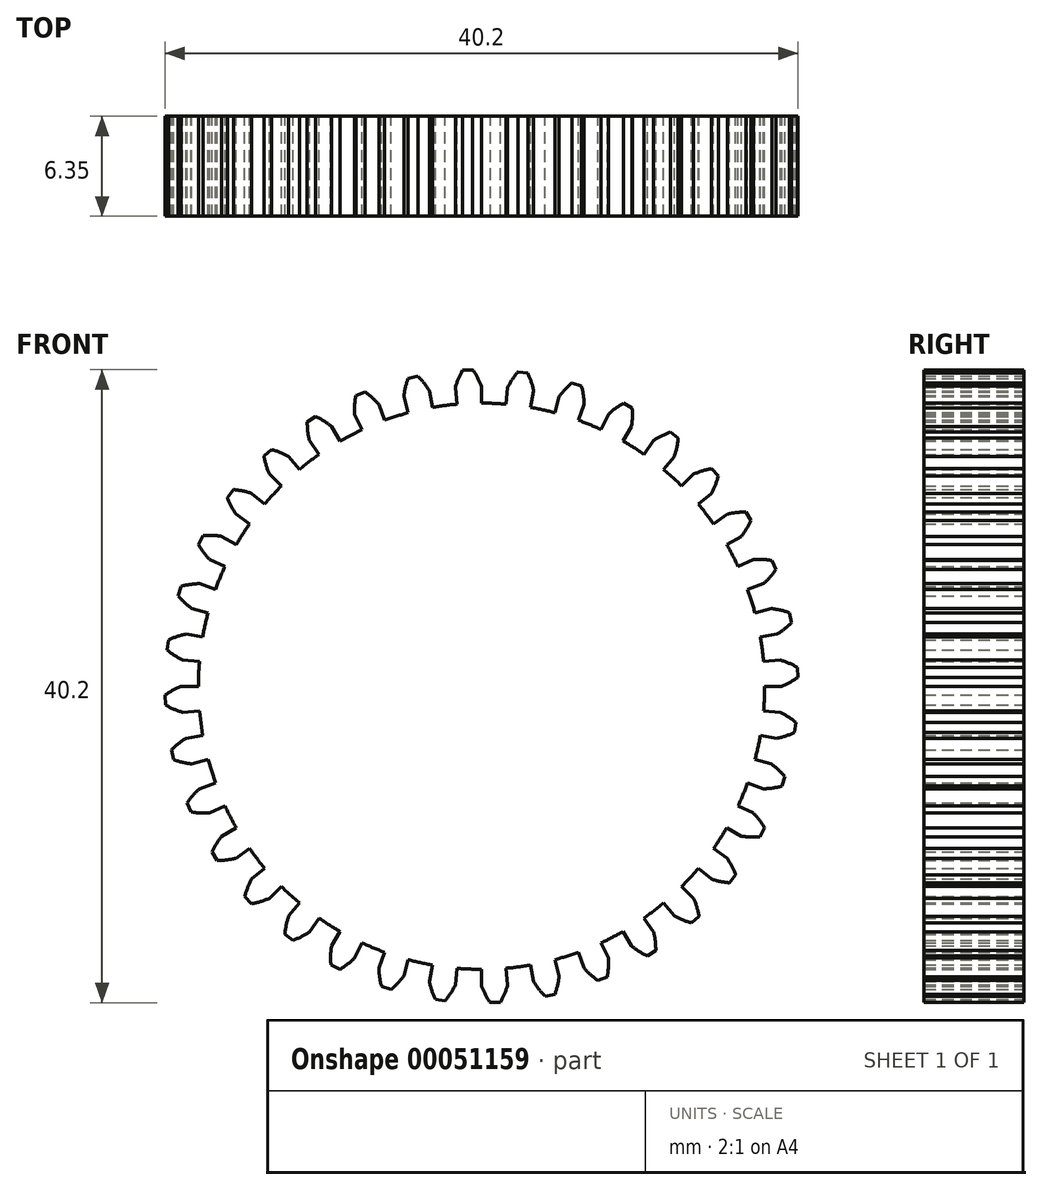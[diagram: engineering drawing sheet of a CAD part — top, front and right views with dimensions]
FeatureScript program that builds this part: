
annotation { "Feature Type Name" : "Feature", "Feature Type Description" : "" }
export const myFeature = defineFeature(function(context is Context, id is Id, definition is map)
    precondition{}
    {
        {
            var Q0;
            Q0=qCreatedBy(makeId("Front.planeOp"),FACE);
            var sketch = newSketch(context, id + "F0", { "sketchPlane" : qUnion([Q0])});
            skArc(sketch, "E0", {"start": v(1.57, 17.91) * mm, "mid": v(0.78, 17.97) * mm, "end": v(0, 17.98) * mm});
            skLineSegment(sketch, "E1", {"start": v(0, 19.05) * mm, "end": v(0, 17.98) * mm, "construction": true});
            skArc(sketch, "E2", {"start": v(-4.48, 17.42) * mm, "mid": v(-4.46, 17.38) * mm, "end": v(-4.45, 17.34) * mm});
            skArc(sketch, "E3.trimOffspring", {"start": v(0, 19.05) * mm, "mid": v(-0.25, 19.6) * mm, "end": v(-0.56, 20.1) * mm});
            skLineSegment(sketch, "E4", {"start": v(-0.56, 20.1) * mm, "end": v(-0.88, 20.08) * mm});
            skLineSegment(sketch, "E5", {"start": v(0, 19.05) * mm, "end": v(0, 17.98) * mm});
            skLineSegment(sketch, "E6.MirrorCS", {"start": v(-1.2, 20.07) * mm, "end": v(-0.88, 20.08) * mm});
            skArc(sketch, "E7.MirrorCS", {"start": v(-1.66, 18.98) * mm, "mid": v(-1.46, 19.54) * mm, "end": v(-1.2, 20.07) * mm});
            skLineSegment(sketch, "E8.MirrorCS", {"start": v(-1.66, 18.98) * mm, "end": v(-1.57, 17.91) * mm});
            skArc(sketch, "E9.1.0", {"start": v(-3.3, 18.76) * mm, "mid": v(-3.65, 19.25) * mm, "end": v(-4.04, 19.7) * mm});
            skLineSegment(sketch, "E9.1.1", {"start": v(-4.04, 19.7) * mm, "end": v(-4.35, 19.63) * mm});
            skLineSegment(sketch, "E9.1.2", {"start": v(-4.66, 19.56) * mm, "end": v(-4.35, 19.63) * mm});
            skArc(sketch, "E9.1.3", {"start": v(-4.93, 18.4) * mm, "mid": v(-4.83, 18.99) * mm, "end": v(-4.66, 19.56) * mm});
            skLineSegment(sketch, "E9.1.4", {"start": v(-4.93, 18.4) * mm, "end": v(-4.65, 17.37) * mm});
            skLineSegment(sketch, "E9.1.5", {"start": v(-3.3, 18.76) * mm, "end": v(-3.12, 17.7) * mm});
            skArc(sketch, "E9.2.0", {"start": v(-6.52, 17.9) * mm, "mid": v(-6.93, 18.32) * mm, "end": v(-7.4, 18.7) * mm});
            skLineSegment(sketch, "E9.2.1", {"start": v(-7.4, 18.7) * mm, "end": v(-7.7, 18.57) * mm});
            skLineSegment(sketch, "E9.2.2", {"start": v(-7.98, 18.45) * mm, "end": v(-7.7, 18.57) * mm});
            skArc(sketch, "E9.2.3", {"start": v(-8.05, 17.27) * mm, "mid": v(-8.05, 17.86) * mm, "end": v(-7.98, 18.45) * mm});
            skLineSegment(sketch, "E9.2.4", {"start": v(-8.05, 17.27) * mm, "end": v(-7.6, 16.3) * mm});
            skLineSegment(sketch, "E9.2.5", {"start": v(-6.52, 17.9) * mm, "end": v(-6.15, 16.9) * mm});
            skArc(sketch, "E9.3.0", {"start": v(-9.52, 16.5) * mm, "mid": v(-10, 16.84) * mm, "end": v(-10.53, 17.12) * mm});
            skLineSegment(sketch, "E9.3.1", {"start": v(-10.53, 17.12) * mm, "end": v(-10.8, 16.95) * mm});
            skLineSegment(sketch, "E9.3.2", {"start": v(-11.07, 16.78) * mm, "end": v(-10.8, 16.95) * mm});
            skArc(sketch, "E9.3.3", {"start": v(-10.93, 15.6) * mm, "mid": v(-11.03, 16.19) * mm, "end": v(-11.07, 16.78) * mm});
            skLineSegment(sketch, "E9.3.4", {"start": v(-10.93, 15.6) * mm, "end": v(-10.31, 14.73) * mm});
            skLineSegment(sketch, "E9.3.5", {"start": v(-9.52, 16.5) * mm, "end": v(-9, 15.57) * mm});
            skArc(sketch, "E9.4.0", {"start": v(-12.25, 14.6) * mm, "mid": v(-12.78, 14.85) * mm, "end": v(-13.35, 15.03) * mm});
            skLineSegment(sketch, "E9.4.1", {"start": v(-13.35, 15.03) * mm, "end": v(-13.58, 14.82) * mm});
            skLineSegment(sketch, "E9.4.2", {"start": v(-13.81, 14.6) * mm, "end": v(-13.58, 14.82) * mm});
            skArc(sketch, "E9.4.3", {"start": v(-13.47, 13.47) * mm, "mid": v(-13.68, 14.03) * mm, "end": v(-13.81, 14.6) * mm});
            skLineSegment(sketch, "E9.4.4", {"start": v(-13.47, 13.47) * mm, "end": v(-12.72, 12.72) * mm});
            skLineSegment(sketch, "E9.4.5", {"start": v(-12.25, 14.6) * mm, "end": v(-11.56, 13.78) * mm});
            skArc(sketch, "E9.5.0", {"start": v(-14.6, 12.25) * mm, "mid": v(-15.17, 12.4) * mm, "end": v(-15.76, 12.49) * mm});
            skLineSegment(sketch, "E9.5.1", {"start": v(-15.76, 12.49) * mm, "end": v(-15.95, 12.24) * mm});
            skLineSegment(sketch, "E9.5.2", {"start": v(-16.14, 11.99) * mm, "end": v(-15.95, 12.24) * mm});
            skArc(sketch, "E9.5.3", {"start": v(-15.6, 10.93) * mm, "mid": v(-15.9, 11.44) * mm, "end": v(-16.14, 11.99) * mm});
            skLineSegment(sketch, "E9.5.4", {"start": v(-15.6, 10.93) * mm, "end": v(-14.73, 10.31) * mm});
            skLineSegment(sketch, "E9.5.5", {"start": v(-14.6, 12.25) * mm, "end": v(-13.78, 11.56) * mm});
            skArc(sketch, "E9.6.0", {"start": v(-16.5, 9.53) * mm, "mid": v(-17.09, 9.58) * mm, "end": v(-17.68, 9.56) * mm});
            skLineSegment(sketch, "E9.6.1", {"start": v(-17.68, 9.56) * mm, "end": v(-17.83, 9.28) * mm});
            skLineSegment(sketch, "E9.6.2", {"start": v(-17.98, 9) * mm, "end": v(-17.83, 9.28) * mm});
            skArc(sketch, "E9.6.3", {"start": v(-17.27, 8.05) * mm, "mid": v(-17.65, 8.5) * mm, "end": v(-17.98, 9) * mm});
            skLineSegment(sketch, "E9.6.4", {"start": v(-17.27, 8.05) * mm, "end": v(-16.3, 7.6) * mm});
            skLineSegment(sketch, "E9.6.5", {"start": v(-16.5, 9.53) * mm, "end": v(-15.57, 9) * mm});
            skArc(sketch, "E9.7.0", {"start": v(-17.9, 6.52) * mm, "mid": v(-18.5, 6.47) * mm, "end": v(-19.08, 6.35) * mm});
            skLineSegment(sketch, "E9.7.1", {"start": v(-19.08, 6.35) * mm, "end": v(-19.17, 6.04) * mm});
            skLineSegment(sketch, "E9.7.2", {"start": v(-19.27, 5.74) * mm, "end": v(-19.17, 6.04) * mm});
            skArc(sketch, "E9.7.3", {"start": v(-18.4, 4.93) * mm, "mid": v(-18.86, 5.3) * mm, "end": v(-19.27, 5.74) * mm});
            skLineSegment(sketch, "E9.7.4", {"start": v(-18.4, 4.93) * mm, "end": v(-17.37, 4.65) * mm});
            skLineSegment(sketch, "E9.7.5", {"start": v(-17.9, 6.52) * mm, "end": v(-16.9, 6.15) * mm});
            skArc(sketch, "E9.8.0", {"start": v(-18.76, 3.3) * mm, "mid": v(-19.34, 3.16) * mm, "end": v(-19.89, 2.94) * mm});
            skLineSegment(sketch, "E9.8.1", {"start": v(-19.89, 2.94) * mm, "end": v(-19.93, 2.62) * mm});
            skLineSegment(sketch, "E9.8.2", {"start": v(-19.97, 2.31) * mm, "end": v(-19.93, 2.62) * mm});
            skArc(sketch, "E9.8.3", {"start": v(-18.98, 1.66) * mm, "mid": v(-19.5, 1.95) * mm, "end": v(-19.97, 2.31) * mm});
            skLineSegment(sketch, "E9.8.4", {"start": v(-18.98, 1.66) * mm, "end": v(-17.91, 1.57) * mm});
            skLineSegment(sketch, "E9.8.5", {"start": v(-18.76, 3.3) * mm, "end": v(-17.7, 3.12) * mm});
            skArc(sketch, "E9.9.0", {"start": v(-19.05, 0) * mm, "mid": v(-19.6, -0.25) * mm, "end": v(-20.1, -0.56) * mm});
            skLineSegment(sketch, "E9.9.1", {"start": v(-20.1, -0.56) * mm, "end": v(-20.08, -0.88) * mm});
            skLineSegment(sketch, "E9.9.2", {"start": v(-20.07, -1.2) * mm, "end": v(-20.08, -0.88) * mm});
            skArc(sketch, "E9.9.3", {"start": v(-18.98, -1.66) * mm, "mid": v(-19.54, -1.46) * mm, "end": v(-20.07, -1.2) * mm});
            skLineSegment(sketch, "E9.9.4", {"start": v(-18.98, -1.66) * mm, "end": v(-17.91, -1.57) * mm});
            skLineSegment(sketch, "E9.9.5", {"start": v(-19.05, 0) * mm, "end": v(-17.98, 0) * mm});
            skArc(sketch, "E9.10.0", {"start": v(-18.76, -3.3) * mm, "mid": v(-19.25, -3.65) * mm, "end": v(-19.7, -4.04) * mm});
            skLineSegment(sketch, "E9.10.1", {"start": v(-19.7, -4.04) * mm, "end": v(-19.63, -4.35) * mm});
            skLineSegment(sketch, "E9.10.2", {"start": v(-19.56, -4.66) * mm, "end": v(-19.63, -4.35) * mm});
            skArc(sketch, "E9.10.3", {"start": v(-18.4, -4.93) * mm, "mid": v(-18.99, -4.83) * mm, "end": v(-19.56, -4.66) * mm});
            skLineSegment(sketch, "E9.10.4", {"start": v(-18.4, -4.93) * mm, "end": v(-17.37, -4.65) * mm});
            skLineSegment(sketch, "E9.10.5", {"start": v(-18.76, -3.3) * mm, "end": v(-17.7, -3.12) * mm});
            skArc(sketch, "E9.11.0", {"start": v(-17.9, -6.52) * mm, "mid": v(-18.32, -6.93) * mm, "end": v(-18.7, -7.4) * mm});
            skLineSegment(sketch, "E9.11.1", {"start": v(-18.7, -7.4) * mm, "end": v(-18.57, -7.7) * mm});
            skLineSegment(sketch, "E9.11.2", {"start": v(-18.45, -7.98) * mm, "end": v(-18.57, -7.7) * mm});
            skArc(sketch, "E9.11.3", {"start": v(-17.27, -8.05) * mm, "mid": v(-17.86, -8.05) * mm, "end": v(-18.45, -7.98) * mm});
            skLineSegment(sketch, "E9.11.4", {"start": v(-17.27, -8.05) * mm, "end": v(-16.3, -7.6) * mm});
            skLineSegment(sketch, "E9.11.5", {"start": v(-17.9, -6.52) * mm, "end": v(-16.9, -6.15) * mm});
            skArc(sketch, "E9.12.0", {"start": v(-16.5, -9.52) * mm, "mid": v(-16.84, -10) * mm, "end": v(-17.12, -10.53) * mm});
            skLineSegment(sketch, "E9.12.1", {"start": v(-17.12, -10.53) * mm, "end": v(-16.95, -10.8) * mm});
            skLineSegment(sketch, "E9.12.2", {"start": v(-16.78, -11.07) * mm, "end": v(-16.95, -10.8) * mm});
            skArc(sketch, "E9.12.3", {"start": v(-15.6, -10.93) * mm, "mid": v(-16.19, -11.03) * mm, "end": v(-16.78, -11.07) * mm});
            skLineSegment(sketch, "E9.12.4", {"start": v(-15.6, -10.93) * mm, "end": v(-14.73, -10.31) * mm});
            skLineSegment(sketch, "E9.12.5", {"start": v(-16.5, -9.52) * mm, "end": v(-15.57, -9) * mm});
            skArc(sketch, "E9.13.0", {"start": v(-14.6, -12.25) * mm, "mid": v(-14.85, -12.78) * mm, "end": v(-15.03, -13.35) * mm});
            skLineSegment(sketch, "E9.13.1", {"start": v(-15.03, -13.35) * mm, "end": v(-14.82, -13.58) * mm});
            skLineSegment(sketch, "E9.13.2", {"start": v(-14.6, -13.81) * mm, "end": v(-14.82, -13.58) * mm});
            skArc(sketch, "E9.13.3", {"start": v(-13.47, -13.47) * mm, "mid": v(-14.03, -13.68) * mm, "end": v(-14.6, -13.81) * mm});
            skLineSegment(sketch, "E9.13.4", {"start": v(-13.47, -13.47) * mm, "end": v(-12.72, -12.72) * mm});
            skLineSegment(sketch, "E9.13.5", {"start": v(-14.6, -12.25) * mm, "end": v(-13.78, -11.56) * mm});
            skArc(sketch, "E9.14.0", {"start": v(-12.25, -14.6) * mm, "mid": v(-12.4, -15.17) * mm, "end": v(-12.49, -15.76) * mm});
            skLineSegment(sketch, "E9.14.1", {"start": v(-12.49, -15.76) * mm, "end": v(-12.24, -15.95) * mm});
            skLineSegment(sketch, "E9.14.2", {"start": v(-11.99, -16.14) * mm, "end": v(-12.24, -15.95) * mm});
            skArc(sketch, "E9.14.3", {"start": v(-10.93, -15.6) * mm, "mid": v(-11.44, -15.9) * mm, "end": v(-11.99, -16.14) * mm});
            skLineSegment(sketch, "E9.14.4", {"start": v(-10.93, -15.6) * mm, "end": v(-10.31, -14.73) * mm});
            skLineSegment(sketch, "E9.14.5", {"start": v(-12.25, -14.6) * mm, "end": v(-11.56, -13.78) * mm});
            skArc(sketch, "E9.15.0", {"start": v(-9.53, -16.5) * mm, "mid": v(-9.58, -17.09) * mm, "end": v(-9.56, -17.68) * mm});
            skLineSegment(sketch, "E9.15.1", {"start": v(-9.56, -17.68) * mm, "end": v(-9.28, -17.83) * mm});
            skLineSegment(sketch, "E9.15.2", {"start": v(-9, -17.98) * mm, "end": v(-9.28, -17.83) * mm});
            skArc(sketch, "E9.15.3", {"start": v(-8.05, -17.27) * mm, "mid": v(-8.5, -17.65) * mm, "end": v(-9, -17.98) * mm});
            skLineSegment(sketch, "E9.15.4", {"start": v(-8.05, -17.27) * mm, "end": v(-7.6, -16.3) * mm});
            skLineSegment(sketch, "E9.15.5", {"start": v(-9.53, -16.5) * mm, "end": v(-9, -15.57) * mm});
            skArc(sketch, "E9.16.0", {"start": v(-6.52, -17.9) * mm, "mid": v(-6.47, -18.5) * mm, "end": v(-6.35, -19.08) * mm});
            skLineSegment(sketch, "E9.16.1", {"start": v(-6.35, -19.08) * mm, "end": v(-6.04, -19.17) * mm});
            skLineSegment(sketch, "E9.16.2", {"start": v(-5.74, -19.27) * mm, "end": v(-6.04, -19.17) * mm});
            skArc(sketch, "E9.16.3", {"start": v(-4.93, -18.4) * mm, "mid": v(-5.3, -18.86) * mm, "end": v(-5.74, -19.27) * mm});
            skLineSegment(sketch, "E9.16.4", {"start": v(-4.93, -18.4) * mm, "end": v(-4.65, -17.37) * mm});
            skLineSegment(sketch, "E9.16.5", {"start": v(-6.52, -17.9) * mm, "end": v(-6.15, -16.9) * mm});
            skArc(sketch, "E9.17.0", {"start": v(-3.3, -18.76) * mm, "mid": v(-3.16, -19.34) * mm, "end": v(-2.94, -19.89) * mm});
            skLineSegment(sketch, "E9.17.1", {"start": v(-2.94, -19.89) * mm, "end": v(-2.62, -19.93) * mm});
            skLineSegment(sketch, "E9.17.2", {"start": v(-2.31, -19.97) * mm, "end": v(-2.62, -19.93) * mm});
            skArc(sketch, "E9.17.3", {"start": v(-1.66, -18.98) * mm, "mid": v(-1.95, -19.5) * mm, "end": v(-2.31, -19.97) * mm});
            skLineSegment(sketch, "E9.17.4", {"start": v(-1.66, -18.98) * mm, "end": v(-1.57, -17.91) * mm});
            skLineSegment(sketch, "E9.17.5", {"start": v(-3.3, -18.76) * mm, "end": v(-3.12, -17.7) * mm});
            skArc(sketch, "E9.18.0", {"start": v(0, -19.05) * mm, "mid": v(0.25, -19.6) * mm, "end": v(0.56, -20.1) * mm});
            skLineSegment(sketch, "E9.18.1", {"start": v(0.56, -20.1) * mm, "end": v(0.88, -20.08) * mm});
            skLineSegment(sketch, "E9.18.2", {"start": v(1.2, -20.07) * mm, "end": v(0.88, -20.08) * mm});
            skArc(sketch, "E9.18.3", {"start": v(1.66, -18.98) * mm, "mid": v(1.46, -19.54) * mm, "end": v(1.2, -20.07) * mm});
            skLineSegment(sketch, "E9.18.4", {"start": v(1.66, -18.98) * mm, "end": v(1.57, -17.91) * mm});
            skLineSegment(sketch, "E9.18.5", {"start": v(0, -19.05) * mm, "end": v(0, -17.98) * mm});
            skArc(sketch, "E9.19.0", {"start": v(3.3, -18.76) * mm, "mid": v(3.65, -19.25) * mm, "end": v(4.04, -19.7) * mm});
            skLineSegment(sketch, "E9.19.1", {"start": v(4.04, -19.7) * mm, "end": v(4.35, -19.63) * mm});
            skLineSegment(sketch, "E9.19.2", {"start": v(4.66, -19.56) * mm, "end": v(4.35, -19.63) * mm});
            skArc(sketch, "E9.19.3", {"start": v(4.93, -18.4) * mm, "mid": v(4.83, -18.99) * mm, "end": v(4.66, -19.56) * mm});
            skLineSegment(sketch, "E9.19.4", {"start": v(4.93, -18.4) * mm, "end": v(4.65, -17.37) * mm});
            skLineSegment(sketch, "E9.19.5", {"start": v(3.3, -18.76) * mm, "end": v(3.12, -17.7) * mm});
            skArc(sketch, "E9.20.0", {"start": v(6.52, -17.9) * mm, "mid": v(6.93, -18.32) * mm, "end": v(7.4, -18.7) * mm});
            skLineSegment(sketch, "E9.20.1", {"start": v(7.4, -18.7) * mm, "end": v(7.7, -18.57) * mm});
            skLineSegment(sketch, "E9.20.2", {"start": v(7.98, -18.45) * mm, "end": v(7.7, -18.57) * mm});
            skArc(sketch, "E9.20.3", {"start": v(8.05, -17.27) * mm, "mid": v(8.05, -17.86) * mm, "end": v(7.98, -18.45) * mm});
            skLineSegment(sketch, "E9.20.4", {"start": v(8.05, -17.27) * mm, "end": v(7.6, -16.3) * mm});
            skLineSegment(sketch, "E9.20.5", {"start": v(6.52, -17.9) * mm, "end": v(6.15, -16.9) * mm});
            skArc(sketch, "E9.21.0", {"start": v(9.53, -16.5) * mm, "mid": v(10, -16.84) * mm, "end": v(10.53, -17.12) * mm});
            skLineSegment(sketch, "E9.21.1", {"start": v(10.53, -17.12) * mm, "end": v(10.8, -16.95) * mm});
            skLineSegment(sketch, "E9.21.2", {"start": v(11.07, -16.78) * mm, "end": v(10.8, -16.95) * mm});
            skArc(sketch, "E9.21.3", {"start": v(10.93, -15.6) * mm, "mid": v(11.03, -16.19) * mm, "end": v(11.07, -16.78) * mm});
            skLineSegment(sketch, "E9.21.4", {"start": v(10.93, -15.6) * mm, "end": v(10.31, -14.73) * mm});
            skLineSegment(sketch, "E9.21.5", {"start": v(9.53, -16.5) * mm, "end": v(9, -15.57) * mm});
            skArc(sketch, "E9.22.0", {"start": v(12.25, -14.6) * mm, "mid": v(12.78, -14.85) * mm, "end": v(13.35, -15.03) * mm});
            skLineSegment(sketch, "E9.22.1", {"start": v(13.35, -15.03) * mm, "end": v(13.58, -14.82) * mm});
            skLineSegment(sketch, "E9.22.2", {"start": v(13.81, -14.6) * mm, "end": v(13.58, -14.82) * mm});
            skArc(sketch, "E9.22.3", {"start": v(13.47, -13.47) * mm, "mid": v(13.68, -14.03) * mm, "end": v(13.81, -14.6) * mm});
            skLineSegment(sketch, "E9.22.4", {"start": v(13.47, -13.47) * mm, "end": v(12.72, -12.72) * mm});
            skLineSegment(sketch, "E9.22.5", {"start": v(12.25, -14.6) * mm, "end": v(11.56, -13.78) * mm});
            skArc(sketch, "E9.23.0", {"start": v(14.6, -12.25) * mm, "mid": v(15.17, -12.4) * mm, "end": v(15.76, -12.49) * mm});
            skLineSegment(sketch, "E9.23.1", {"start": v(15.76, -12.49) * mm, "end": v(15.95, -12.24) * mm});
            skLineSegment(sketch, "E9.23.2", {"start": v(16.14, -11.99) * mm, "end": v(15.95, -12.24) * mm});
            skArc(sketch, "E9.23.3", {"start": v(15.6, -10.93) * mm, "mid": v(15.9, -11.44) * mm, "end": v(16.14, -11.99) * mm});
            skLineSegment(sketch, "E9.23.4", {"start": v(15.6, -10.93) * mm, "end": v(14.73, -10.31) * mm});
            skLineSegment(sketch, "E9.23.5", {"start": v(14.6, -12.25) * mm, "end": v(13.78, -11.56) * mm});
            skArc(sketch, "E9.24.0", {"start": v(16.5, -9.53) * mm, "mid": v(17.09, -9.58) * mm, "end": v(17.68, -9.56) * mm});
            skLineSegment(sketch, "E9.24.1", {"start": v(17.68, -9.56) * mm, "end": v(17.83, -9.28) * mm});
            skLineSegment(sketch, "E9.24.2", {"start": v(17.98, -9) * mm, "end": v(17.83, -9.28) * mm});
            skArc(sketch, "E9.24.3", {"start": v(17.27, -8.05) * mm, "mid": v(17.65, -8.5) * mm, "end": v(17.98, -9) * mm});
            skLineSegment(sketch, "E9.24.4", {"start": v(17.27, -8.05) * mm, "end": v(16.3, -7.6) * mm});
            skLineSegment(sketch, "E9.24.5", {"start": v(16.5, -9.53) * mm, "end": v(15.57, -9) * mm});
            skArc(sketch, "E9.25.0", {"start": v(17.9, -6.52) * mm, "mid": v(18.5, -6.47) * mm, "end": v(19.08, -6.35) * mm});
            skLineSegment(sketch, "E9.25.1", {"start": v(19.08, -6.35) * mm, "end": v(19.17, -6.04) * mm});
            skLineSegment(sketch, "E9.25.2", {"start": v(19.27, -5.74) * mm, "end": v(19.17, -6.04) * mm});
            skArc(sketch, "E9.25.3", {"start": v(18.4, -4.93) * mm, "mid": v(18.86, -5.3) * mm, "end": v(19.27, -5.74) * mm});
            skLineSegment(sketch, "E9.25.4", {"start": v(18.4, -4.93) * mm, "end": v(17.37, -4.65) * mm});
            skLineSegment(sketch, "E9.25.5", {"start": v(17.9, -6.52) * mm, "end": v(16.9, -6.15) * mm});
            skArc(sketch, "E9.26.0", {"start": v(18.76, -3.3) * mm, "mid": v(19.34, -3.16) * mm, "end": v(19.89, -2.94) * mm});
            skLineSegment(sketch, "E9.26.1", {"start": v(19.89, -2.94) * mm, "end": v(19.93, -2.62) * mm});
            skLineSegment(sketch, "E9.26.2", {"start": v(19.97, -2.31) * mm, "end": v(19.93, -2.62) * mm});
            skArc(sketch, "E9.26.3", {"start": v(18.98, -1.66) * mm, "mid": v(19.5, -1.95) * mm, "end": v(19.97, -2.31) * mm});
            skLineSegment(sketch, "E9.26.4", {"start": v(18.98, -1.66) * mm, "end": v(17.91, -1.57) * mm});
            skLineSegment(sketch, "E9.26.5", {"start": v(18.76, -3.3) * mm, "end": v(17.7, -3.12) * mm});
            skArc(sketch, "E9.27.0", {"start": v(19.05, 0) * mm, "mid": v(19.6, 0.25) * mm, "end": v(20.1, 0.56) * mm});
            skLineSegment(sketch, "E9.27.1", {"start": v(20.1, 0.56) * mm, "end": v(20.08, 0.88) * mm});
            skLineSegment(sketch, "E9.27.2", {"start": v(20.07, 1.2) * mm, "end": v(20.08, 0.88) * mm});
            skArc(sketch, "E9.27.3", {"start": v(18.98, 1.66) * mm, "mid": v(19.54, 1.46) * mm, "end": v(20.07, 1.2) * mm});
            skLineSegment(sketch, "E9.27.4", {"start": v(18.98, 1.66) * mm, "end": v(17.91, 1.57) * mm});
            skLineSegment(sketch, "E9.27.5", {"start": v(19.05, 0) * mm, "end": v(17.98, 0) * mm});
            skArc(sketch, "E9.28.0", {"start": v(18.76, 3.3) * mm, "mid": v(19.25, 3.65) * mm, "end": v(19.7, 4.04) * mm});
            skLineSegment(sketch, "E9.28.1", {"start": v(19.7, 4.04) * mm, "end": v(19.63, 4.35) * mm});
            skLineSegment(sketch, "E9.28.2", {"start": v(19.56, 4.66) * mm, "end": v(19.63, 4.35) * mm});
            skArc(sketch, "E9.28.3", {"start": v(18.4, 4.93) * mm, "mid": v(18.99, 4.83) * mm, "end": v(19.56, 4.66) * mm});
            skLineSegment(sketch, "E9.28.4", {"start": v(18.4, 4.93) * mm, "end": v(17.37, 4.65) * mm});
            skLineSegment(sketch, "E9.28.5", {"start": v(18.76, 3.3) * mm, "end": v(17.7, 3.12) * mm});
            skArc(sketch, "E9.29.0", {"start": v(17.9, 6.52) * mm, "mid": v(18.32, 6.93) * mm, "end": v(18.7, 7.4) * mm});
            skLineSegment(sketch, "E9.29.1", {"start": v(18.7, 7.4) * mm, "end": v(18.57, 7.7) * mm});
            skLineSegment(sketch, "E9.29.2", {"start": v(18.45, 7.98) * mm, "end": v(18.57, 7.7) * mm});
            skArc(sketch, "E9.29.3", {"start": v(17.27, 8.05) * mm, "mid": v(17.86, 8.05) * mm, "end": v(18.45, 7.98) * mm});
            skLineSegment(sketch, "E9.29.4", {"start": v(17.27, 8.05) * mm, "end": v(16.3, 7.6) * mm});
            skLineSegment(sketch, "E9.29.5", {"start": v(17.9, 6.52) * mm, "end": v(16.9, 6.15) * mm});
            skArc(sketch, "E9.30.0", {"start": v(16.5, 9.52) * mm, "mid": v(16.84, 10) * mm, "end": v(17.12, 10.53) * mm});
            skLineSegment(sketch, "E9.30.1", {"start": v(17.12, 10.53) * mm, "end": v(16.95, 10.8) * mm});
            skLineSegment(sketch, "E9.30.2", {"start": v(16.78, 11.07) * mm, "end": v(16.95, 10.8) * mm});
            skArc(sketch, "E9.30.3", {"start": v(15.6, 10.93) * mm, "mid": v(16.19, 11.03) * mm, "end": v(16.78, 11.07) * mm});
            skLineSegment(sketch, "E9.30.4", {"start": v(15.6, 10.93) * mm, "end": v(14.73, 10.31) * mm});
            skLineSegment(sketch, "E9.30.5", {"start": v(16.5, 9.52) * mm, "end": v(15.57, 9) * mm});
            skArc(sketch, "E9.31.0", {"start": v(14.6, 12.25) * mm, "mid": v(14.85, 12.78) * mm, "end": v(15.03, 13.35) * mm});
            skLineSegment(sketch, "E9.31.1", {"start": v(15.03, 13.35) * mm, "end": v(14.82, 13.58) * mm});
            skLineSegment(sketch, "E9.31.2", {"start": v(14.6, 13.81) * mm, "end": v(14.82, 13.58) * mm});
            skArc(sketch, "E9.31.3", {"start": v(13.47, 13.47) * mm, "mid": v(14.03, 13.68) * mm, "end": v(14.6, 13.81) * mm});
            skLineSegment(sketch, "E9.31.4", {"start": v(13.47, 13.47) * mm, "end": v(12.72, 12.72) * mm});
            skLineSegment(sketch, "E9.31.5", {"start": v(14.6, 12.25) * mm, "end": v(13.78, 11.56) * mm});
            skArc(sketch, "E9.32.0", {"start": v(12.25, 14.6) * mm, "mid": v(12.4, 15.17) * mm, "end": v(12.49, 15.76) * mm});
            skLineSegment(sketch, "E9.32.1", {"start": v(12.49, 15.76) * mm, "end": v(12.24, 15.95) * mm});
            skLineSegment(sketch, "E9.32.2", {"start": v(11.99, 16.14) * mm, "end": v(12.24, 15.95) * mm});
            skArc(sketch, "E9.32.3", {"start": v(10.93, 15.6) * mm, "mid": v(11.44, 15.9) * mm, "end": v(11.99, 16.14) * mm});
            skLineSegment(sketch, "E9.32.4", {"start": v(10.93, 15.6) * mm, "end": v(10.31, 14.73) * mm});
            skLineSegment(sketch, "E9.32.5", {"start": v(12.25, 14.6) * mm, "end": v(11.56, 13.78) * mm});
            skArc(sketch, "E9.33.0", {"start": v(9.52, 16.5) * mm, "mid": v(9.58, 17.09) * mm, "end": v(9.56, 17.68) * mm});
            skLineSegment(sketch, "E9.33.1", {"start": v(9.56, 17.68) * mm, "end": v(9.28, 17.83) * mm});
            skLineSegment(sketch, "E9.33.2", {"start": v(9, 17.98) * mm, "end": v(9.28, 17.83) * mm});
            skArc(sketch, "E9.33.3", {"start": v(8.05, 17.27) * mm, "mid": v(8.5, 17.65) * mm, "end": v(9, 17.98) * mm});
            skLineSegment(sketch, "E9.33.4", {"start": v(8.05, 17.27) * mm, "end": v(7.6, 16.3) * mm});
            skLineSegment(sketch, "E9.33.5", {"start": v(9.52, 16.5) * mm, "end": v(9, 15.57) * mm});
            skArc(sketch, "E9.34.0", {"start": v(6.52, 17.9) * mm, "mid": v(6.47, 18.5) * mm, "end": v(6.35, 19.08) * mm});
            skLineSegment(sketch, "E9.34.1", {"start": v(6.35, 19.08) * mm, "end": v(6.04, 19.17) * mm});
            skLineSegment(sketch, "E9.34.2", {"start": v(5.74, 19.27) * mm, "end": v(6.04, 19.17) * mm});
            skArc(sketch, "E9.34.3", {"start": v(4.93, 18.4) * mm, "mid": v(5.3, 18.86) * mm, "end": v(5.74, 19.27) * mm});
            skLineSegment(sketch, "E9.34.4", {"start": v(4.93, 18.4) * mm, "end": v(4.65, 17.37) * mm});
            skLineSegment(sketch, "E9.34.5", {"start": v(6.52, 17.9) * mm, "end": v(6.15, 16.9) * mm});
            skArc(sketch, "E9.35.0", {"start": v(3.3, 18.76) * mm, "mid": v(3.16, 19.34) * mm, "end": v(2.94, 19.89) * mm});
            skLineSegment(sketch, "E9.35.1", {"start": v(2.94, 19.89) * mm, "end": v(2.62, 19.93) * mm});
            skLineSegment(sketch, "E9.35.2", {"start": v(2.31, 19.97) * mm, "end": v(2.62, 19.93) * mm});
            skArc(sketch, "E9.35.3", {"start": v(1.66, 18.98) * mm, "mid": v(1.95, 19.5) * mm, "end": v(2.31, 19.97) * mm});
            skLineSegment(sketch, "E9.35.4", {"start": v(1.66, 18.98) * mm, "end": v(1.57, 17.91) * mm});
            skLineSegment(sketch, "E9.35.5", {"start": v(3.3, 18.76) * mm, "end": v(3.12, 17.7) * mm});
            skArc(sketch, "E10.trimOffspring", {"start": v(-4.44, 17.34) * mm, "mid": v(-4.44, 17.34) * mm, "end": v(-4.45, 17.34) * mm});
            skArc(sketch, "E11.trimOffspring", {"start": v(-1.57, 17.91) * mm, "mid": v(-2.35, 17.83) * mm, "end": v(-3.12, 17.7) * mm});
            skArc(sketch, "E12.trimOffspring", {"start": v(-4.47, 17.42) * mm, "mid": v(-5.32, 17.18) * mm, "end": v(-6.15, 16.9) * mm});
            skArc(sketch, "E13.trimOffspring", {"start": v(-4.04, 19.7) * mm, "mid": v(-4.4, 19.62) * mm, "end": v(-4.74, 19.54) * mm});
            skArc(sketch, "E14.trimOffspring", {"start": v(-0.56, 20.1) * mm, "mid": v(-0.88, 20.08) * mm, "end": v(-1.2, 20.07) * mm});
            skArc(sketch, "E15.trimOffspring", {"start": v(4.45, 17.34) * mm, "mid": v(4.46, 17.38) * mm, "end": v(4.47, 17.42) * mm});
            skArc(sketch, "E16.trimOffspring", {"start": v(-10.31, 14.73) * mm, "mid": v(-10.95, 14.27) * mm, "end": v(-11.56, 13.78) * mm});
            skArc(sketch, "E17.trimOffspring", {"start": v(-14.73, 10.31) * mm, "mid": v(-15.17, 9.66) * mm, "end": v(-15.57, 9) * mm});
            skArc(sketch, "E18.trimOffspring", {"start": v(-16.3, 7.6) * mm, "mid": v(-16.61, 6.88) * mm, "end": v(-16.9, 6.15) * mm});
            skArc(sketch, "E19.trimOffspring", {"start": v(-17.37, 4.65) * mm, "mid": v(-17.56, 3.9) * mm, "end": v(-17.7, 3.12) * mm});
            skArc(sketch, "E20.trimOffspring", {"start": v(-17.91, 1.57) * mm, "mid": v(-17.97, 0.78) * mm, "end": v(-17.98, 0) * mm});
            skArc(sketch, "E21.trimOffspring", {"start": v(-16.3, -7.6) * mm, "mid": v(-15.95, -8.3) * mm, "end": v(-15.57, -9) * mm});
            skArc(sketch, "E22.trimOffspring", {"start": v(-14.73, -10.31) * mm, "mid": v(-14.27, -10.95) * mm, "end": v(-13.78, -11.56) * mm});
            skArc(sketch, "E23.trimOffspring", {"start": v(-12.72, -12.72) * mm, "mid": v(-12.15, -13.26) * mm, "end": v(-11.56, -13.78) * mm});
            skArc(sketch, "E24.trimOffspring", {"start": v(4.65, 17.37) * mm, "mid": v(3.9, 17.56) * mm, "end": v(3.12, 17.7) * mm});
            skArc(sketch, "E25.trimOffspring", {"start": v(7.6, 16.3) * mm, "mid": v(6.88, 16.61) * mm, "end": v(6.15, 16.9) * mm});
            skArc(sketch, "E26.trimOffspring", {"start": v(10.31, 14.73) * mm, "mid": v(9.66, 15.17) * mm, "end": v(9, 15.57) * mm});
            skArc(sketch, "E27.trimOffspring", {"start": v(12.72, 12.72) * mm, "mid": v(12.15, 13.26) * mm, "end": v(11.56, 13.78) * mm});
            skArc(sketch, "E28.trimOffspring", {"start": v(14.73, 10.31) * mm, "mid": v(14.27, 10.95) * mm, "end": v(13.78, 11.56) * mm});
            skArc(sketch, "E29.trimOffspring", {"start": v(16.3, 7.6) * mm, "mid": v(15.95, 8.3) * mm, "end": v(15.57, 9) * mm});
            skArc(sketch, "E30.trimOffspring", {"start": v(17.37, 4.65) * mm, "mid": v(17.15, 5.4) * mm, "end": v(16.9, 6.15) * mm});
            skArc(sketch, "E31.trimOffspring", {"start": v(17.91, 1.57) * mm, "mid": v(17.83, 2.35) * mm, "end": v(17.7, 3.12) * mm});
            skArc(sketch, "E32.trimOffspring", {"start": v(17.91, -1.57) * mm, "mid": v(17.97, -0.78) * mm, "end": v(17.98, 0) * mm});
            skArc(sketch, "E33.trimOffspring", {"start": v(17.37, -4.65) * mm, "mid": v(17.56, -3.9) * mm, "end": v(17.7, -3.12) * mm});
            skArc(sketch, "E34.trimOffspring", {"start": v(16.3, -7.6) * mm, "mid": v(16.61, -6.88) * mm, "end": v(16.9, -6.15) * mm});
            skArc(sketch, "E35.trimOffspring", {"start": v(14.73, -10.31) * mm, "mid": v(15.17, -9.66) * mm, "end": v(15.57, -9) * mm});
            skArc(sketch, "E36.trimOffspring", {"start": v(12.72, -12.72) * mm, "mid": v(13.26, -12.15) * mm, "end": v(13.78, -11.56) * mm});
            skArc(sketch, "E37.trimOffspring", {"start": v(10.31, -14.73) * mm, "mid": v(10.95, -14.27) * mm, "end": v(11.56, -13.78) * mm});
            skArc(sketch, "E38.trimOffspring", {"start": v(7.6, -16.3) * mm, "mid": v(8.3, -15.95) * mm, "end": v(9, -15.57) * mm});
            skArc(sketch, "E39.trimOffspring", {"start": v(4.65, -17.37) * mm, "mid": v(5.4, -17.15) * mm, "end": v(6.15, -16.9) * mm});
            skArc(sketch, "E40.trimOffspring", {"start": v(1.57, -17.91) * mm, "mid": v(2.35, -17.83) * mm, "end": v(3.12, -17.7) * mm});
            skArc(sketch, "E41.trimOffspring", {"start": v(-1.57, -17.91) * mm, "mid": v(-0.78, -17.97) * mm, "end": v(0, -17.98) * mm});
            skArc(sketch, "E42.trimOffspring", {"start": v(-4.65, -17.37) * mm, "mid": v(-3.9, -17.56) * mm, "end": v(-3.12, -17.7) * mm});
            skArc(sketch, "E43.trimOffspring", {"start": v(-7.6, -16.3) * mm, "mid": v(-6.88, -16.61) * mm, "end": v(-6.15, -16.9) * mm});
            skArc(sketch, "E44.trimOffspring", {"start": v(-10.31, -14.73) * mm, "mid": v(-9.66, -15.17) * mm, "end": v(-9, -15.57) * mm});
            skArc(sketch, "E45.trimOffspring", {"start": v(-12.72, 12.72) * mm, "mid": v(-13.26, 12.15) * mm, "end": v(-13.78, 11.56) * mm});
            skLineSegment(sketch, "E46", {"start": v(-9, 15.57) * mm, "end": v(-7.6, 16.3) * mm});
            skLineSegment(sketch, "E47", {"start": v(-17.91, -1.57) * mm, "end": v(-17.7, -3.12) * mm});
            skLineSegment(sketch, "E48", {"start": v(-17.37, -4.65) * mm, "end": v(-16.9, -6.15) * mm});
            skSolve(sketch);
        }
        {
            var Q0;
            Q0=qCreatedBy(makeId("Front.planeOp"),FACE);
            var sketch = newSketch(context, id + "F1", { "sketchPlane" : qUnion([Q0])});
            skSolve(sketch);
        }
        {
            var Q0;
            Q0 = qSketchRegion(id + "F1", true);
            var Q1;
            Q1=makeQuery(id+"F0.imprint","IMPRINT",FACE,{"disambiguationData":[TD([[makeQuery(id+"F0.imprint","IMPRINT",EDGE,{"derivedFrom":sQuery(id+"F0.wireOp",EDGE,"E0")}),1.0]])]});
            extrude(context, id + "F2", {"entities" : qUnion([Q0, Q1]), "depth" : 6.35 * mm});
        }
    });
